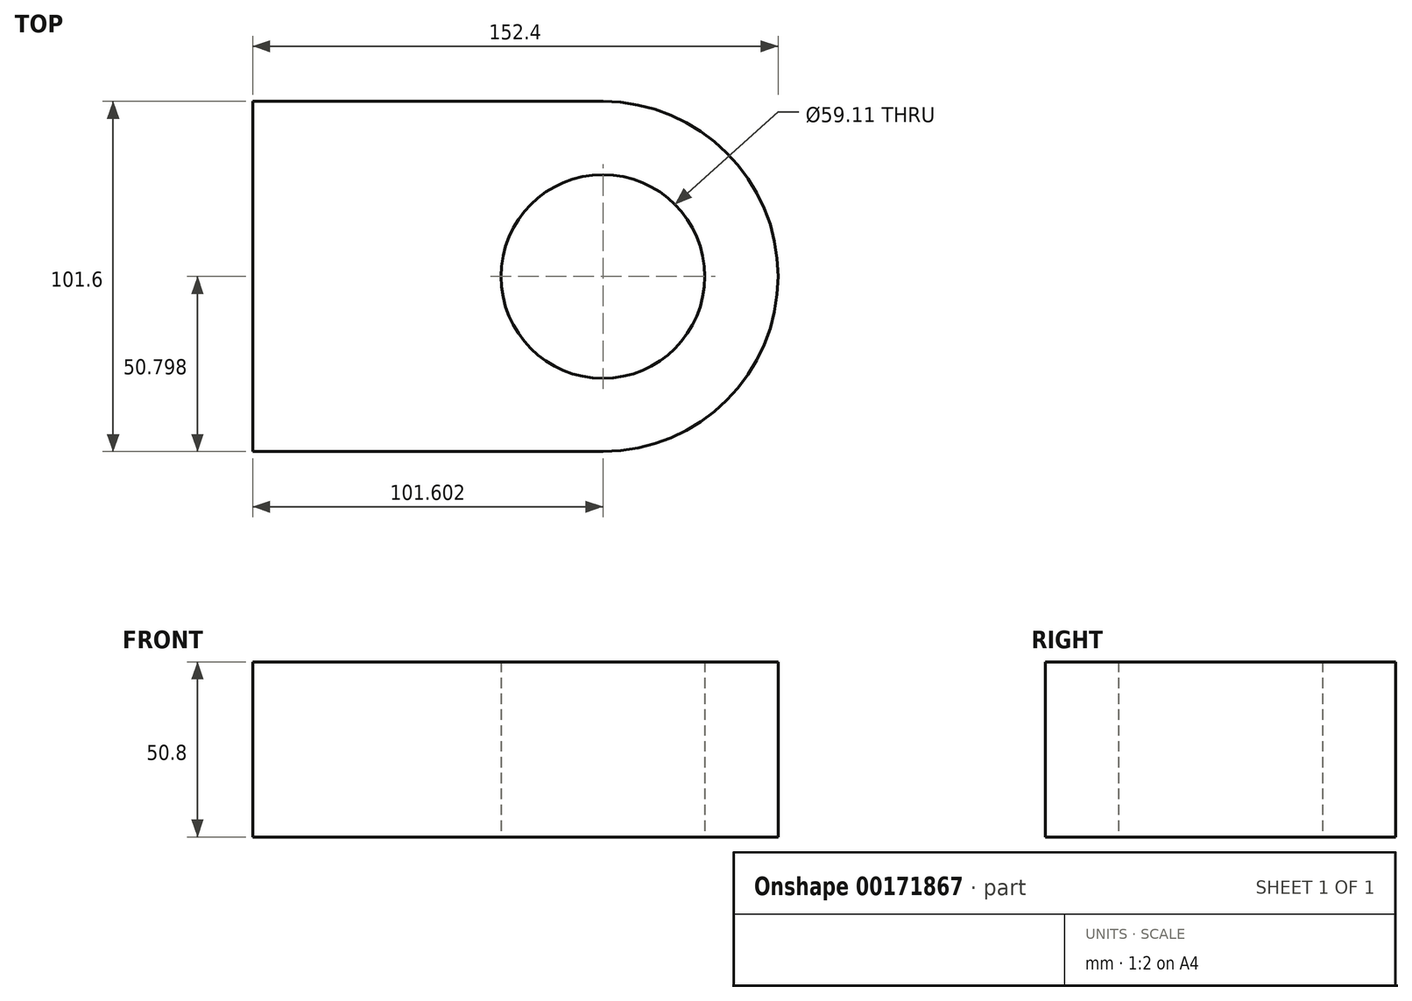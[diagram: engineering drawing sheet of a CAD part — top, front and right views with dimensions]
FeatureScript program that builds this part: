
annotation { "Feature Type Name" : "Feature", "Feature Type Description" : "" }
export const myFeature = defineFeature(function(context is Context, id is Id, definition is map)
    precondition{}
    {
        {
            var Q0;
            Q0=qCreatedBy(makeId("Top.planeOp"),FACE);
            var sketch = newSketch(context, id + "F0", { "sketchPlane" : qUnion([Q0])});
            skLineSegment(sketch, "E0.bottom", {"start": v(-43.32, 67.15) * mm, "end": v(58.28, 67.15) * mm});
            skLineSegment(sketch, "E0.top", {"start": v(-43.32, -34.45) * mm, "end": v(58.28, -34.45) * mm});
            skLineSegment(sketch, "E0.left", {"start": v(-43.32, 67.15) * mm, "end": v(-43.32, -34.45) * mm});
            skLineSegment(sketch, "E0.right", {"start": v(58.28, 67.15) * mm, "end": v(58.28, -34.45) * mm});
            skArc(sketch, "E1", {"start": v(58.28, -34.45) * mm, "mid": v(109.08, 16.35) * mm, "end": v(58.28, 67.15) * mm});
            skCircle(sketch, "E2", {"center": v(58.28, 16.35) * mm, "radius": 29.56 * mm});
            skSolve(sketch);
        }
        {
            var Q0;
            Q0=makeQuery(id+"F0.imprint","IMPRINT",FACE,{"disambiguationData":[TD([[makeQuery(id+"F0.imprint","IMPRINT",EDGE,{"derivedFrom":sQuery(id+"F0.wireOp",EDGE,"E0.bottom")}),-1.0]])]});
            var Q1;
            Q1=makeQuery(id+"F0.imprint","IMPRINT",FACE,{"disambiguationData":[TD([[makeQuery(id+"F0.imprint","IMPRINT",EDGE,{"derivedFrom":sQuery(id+"F0.wireOp",EDGE,"E0.right")}),1.0]])]});
            extrude(context, id + "F1", {"entities" : qUnion([Q0, Q1]), "depth" : 50.8 * mm});
        }
    });
